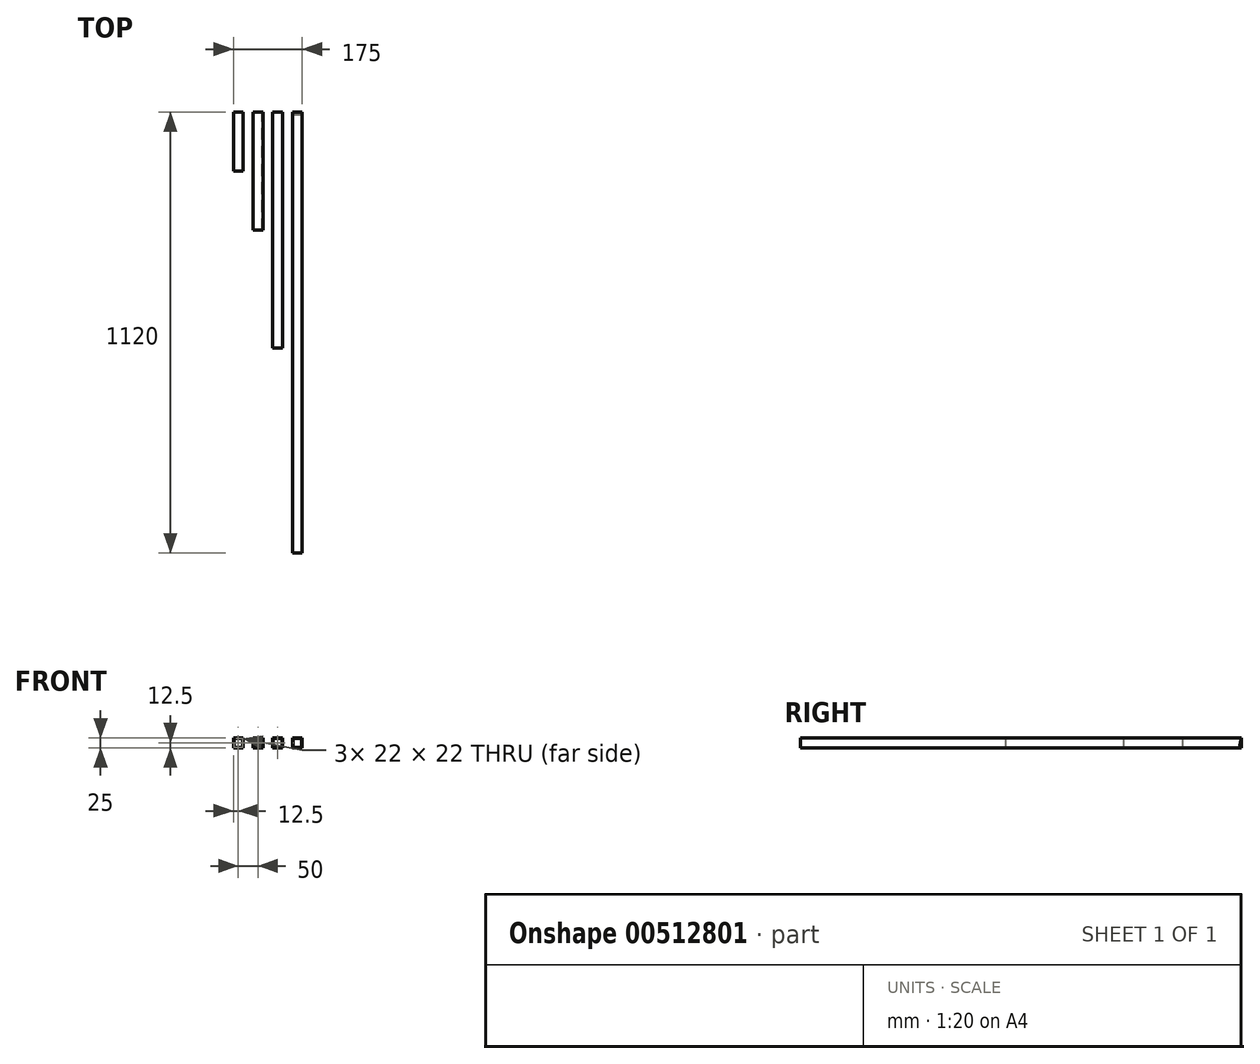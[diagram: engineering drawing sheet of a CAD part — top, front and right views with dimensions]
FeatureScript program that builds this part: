
annotation { "Feature Type Name" : "Feature", "Feature Type Description" : "" }
export const myFeature = defineFeature(function(context is Context, id is Id, definition is map)
    precondition{}
    {
        {
            var Q0;
            Q0=qCreatedBy(makeId("Front.planeOp"),FACE);
            var sketch = newSketch(context, id + "F0", { "sketchPlane" : qUnion([Q0])});
            skLineSegment(sketch, "E0.bottom", {"start": v(12.5, 12.5) * mm, "end": v(-12.5, 12.5) * mm});
            skLineSegment(sketch, "E0.top", {"start": v(12.5, -12.5) * mm, "end": v(-12.5, -12.5) * mm});
            skLineSegment(sketch, "E0.left", {"start": v(12.5, 12.5) * mm, "end": v(12.5, -12.5) * mm});
            skLineSegment(sketch, "E0.right", {"start": v(-12.5, 12.5) * mm, "end": v(-12.5, -12.5) * mm});
            skPoint(sketch, "E0.middle", {"position": v(0, 0) * mm});
            skLineSegment(sketch, "E1.bottom", {"start": v(11, 11) * mm, "end": v(-11, 11) * mm});
            skLineSegment(sketch, "E1.top", {"start": v(11, -11) * mm, "end": v(-11, -11) * mm});
            skLineSegment(sketch, "E1.left", {"start": v(11, 11) * mm, "end": v(11, -11) * mm});
            skLineSegment(sketch, "E1.right", {"start": v(-11, 11) * mm, "end": v(-11, -11) * mm});
            skSolve(sketch);
        }
        {
            var Q0;
            Q0 = qSketchRegion(id + "F0", true);
            extrude(context, id + "F1", {"entities" : qUnion([Q0]), "depth" : 600 * mm});
        }
        {
            var Q0;
            Q0=qCreatedBy(makeId("Front.planeOp"),FACE);
            var sketch = newSketch(context, id + "F2", { "sketchPlane" : qUnion([Q0])});
            skPoint(sketch, "E2", {"position": v(-50, 0) * mm});
            skLineSegment(sketch, "E3.bottom", {"start": v(-62.5, 12.5) * mm, "end": v(-37.5, 12.5) * mm});
            skLineSegment(sketch, "E3.top", {"start": v(-62.5, -12.5) * mm, "end": v(-37.5, -12.5) * mm});
            skLineSegment(sketch, "E3.left", {"start": v(-62.5, 12.5) * mm, "end": v(-62.5, -12.5) * mm});
            skLineSegment(sketch, "E3.right", {"start": v(-37.5, 12.5) * mm, "end": v(-37.5, -12.5) * mm});
            skLineSegment(sketch, "E4.bottom", {"start": v(-61, 11) * mm, "end": v(-39, 11) * mm});
            skLineSegment(sketch, "E4.top", {"start": v(-61, -11) * mm, "end": v(-39, -11) * mm});
            skLineSegment(sketch, "E4.left", {"start": v(-61, 11) * mm, "end": v(-61, -11) * mm});
            skLineSegment(sketch, "E4.right", {"start": v(-39, 11) * mm, "end": v(-39, -11) * mm});
            skSolve(sketch);
        }
        {
            var Q0;
            Q0 = qSketchRegion(id + "F2", true);
            extrude(context, id + "F3", {"entities" : qUnion([Q0]), "depth" : 300 * mm});
        }
        {
            var Q0;
            Q0=qCreatedBy(makeId("Front.planeOp"),FACE);
            var sketch = newSketch(context, id + "F4", { "sketchPlane" : qUnion([Q0])});
            skPoint(sketch, "E5", {"position": v(50, 0) * mm});
            skLineSegment(sketch, "E6.bottom", {"start": v(37.5, 12.5) * mm, "end": v(62.5, 12.5) * mm});
            skLineSegment(sketch, "E6.top", {"start": v(37.5, -12.5) * mm, "end": v(62.5, -12.5) * mm});
            skLineSegment(sketch, "E6.left", {"start": v(37.5, 12.5) * mm, "end": v(37.5, -12.5) * mm});
            skLineSegment(sketch, "E6.right", {"start": v(62.5, 12.5) * mm, "end": v(62.5, -12.5) * mm});
            skLineSegment(sketch, "E7.bottom", {"start": v(39, 11) * mm, "end": v(61, 11) * mm});
            skLineSegment(sketch, "E7.top", {"start": v(39, -11) * mm, "end": v(61, -11) * mm});
            skLineSegment(sketch, "E7.left", {"start": v(39, 11) * mm, "end": v(39, -11) * mm});
            skLineSegment(sketch, "E7.right", {"start": v(61, 11) * mm, "end": v(61, -11) * mm});
            skSolve(sketch);
        }
        {
            var Q0;
            Q0 = qSketchRegion(id + "F4", true);
            extrude(context, id + "F5", {"entities" : qUnion([Q0]), "depth" : 1120 * mm});
        }
        {
            var Q0;
            Q0=makeQuery(id+"F5.opExtrude","SWEPT_FACE",FACE,{"disambiguationData":[OSD([sQuery(id+"F4.wireOp",EDGE,"E6.right")])]});
            var sketch = newSketch(context, id + "F6", { "sketchPlane" : qUnion([Q0])});
            skLineSegment(sketch, "E8", {"start": v(-6, -12.5) * mm, "end": v(0, 12.5) * mm});
            skLineSegment(sketch, "E9.0", {"start": v(0, 12.5) * mm, "end": v(0, -12.5) * mm});
            skLineSegment(sketch, "E10", {"start": v(-6, -12.5) * mm, "end": v(0, -12.5) * mm});
            skSolve(sketch);
        }
        {
            var Q0;
            Q0 = qSketchRegion(id + "F6", true);
            extrude(context, id + "F7", {"entities" : qUnion([Q0]), "operationType" : NewBodyOperationType.REMOVE, "oppositeDirection" : true, "depth" : 25 * mm});
        }
        {
            var Q0;
            Q0=qCreatedBy(makeId("Front.planeOp"),FACE);
            var sketch = newSketch(context, id + "F8", { "sketchPlane" : qUnion([Q0])});
            skPoint(sketch, "E11", {"position": v(-100, 0) * mm});
            skLineSegment(sketch, "E12.bottom", {"start": v(-112.5, 12.5) * mm, "end": v(-87.5, 12.5) * mm});
            skLineSegment(sketch, "E12.top", {"start": v(-112.5, -12.5) * mm, "end": v(-87.5, -12.5) * mm});
            skLineSegment(sketch, "E12.left", {"start": v(-112.5, 12.5) * mm, "end": v(-112.5, -12.5) * mm});
            skLineSegment(sketch, "E12.right", {"start": v(-87.5, 12.5) * mm, "end": v(-87.5, -12.5) * mm});
            skLineSegment(sketch, "E13.bottom", {"start": v(-111, 11) * mm, "end": v(-89, 11) * mm});
            skLineSegment(sketch, "E13.top", {"start": v(-111, -11) * mm, "end": v(-89, -11) * mm});
            skLineSegment(sketch, "E13.left", {"start": v(-111, 11) * mm, "end": v(-111, -11) * mm});
            skLineSegment(sketch, "E13.right", {"start": v(-89, 11) * mm, "end": v(-89, -11) * mm});
            skSolve(sketch);
        }
        {
            var Q0;
            Q0 = qSketchRegion(id + "F8", true);
            extrude(context, id + "F9", {"entities" : qUnion([Q0]), "depth" : 150 * mm});
        }
    });
